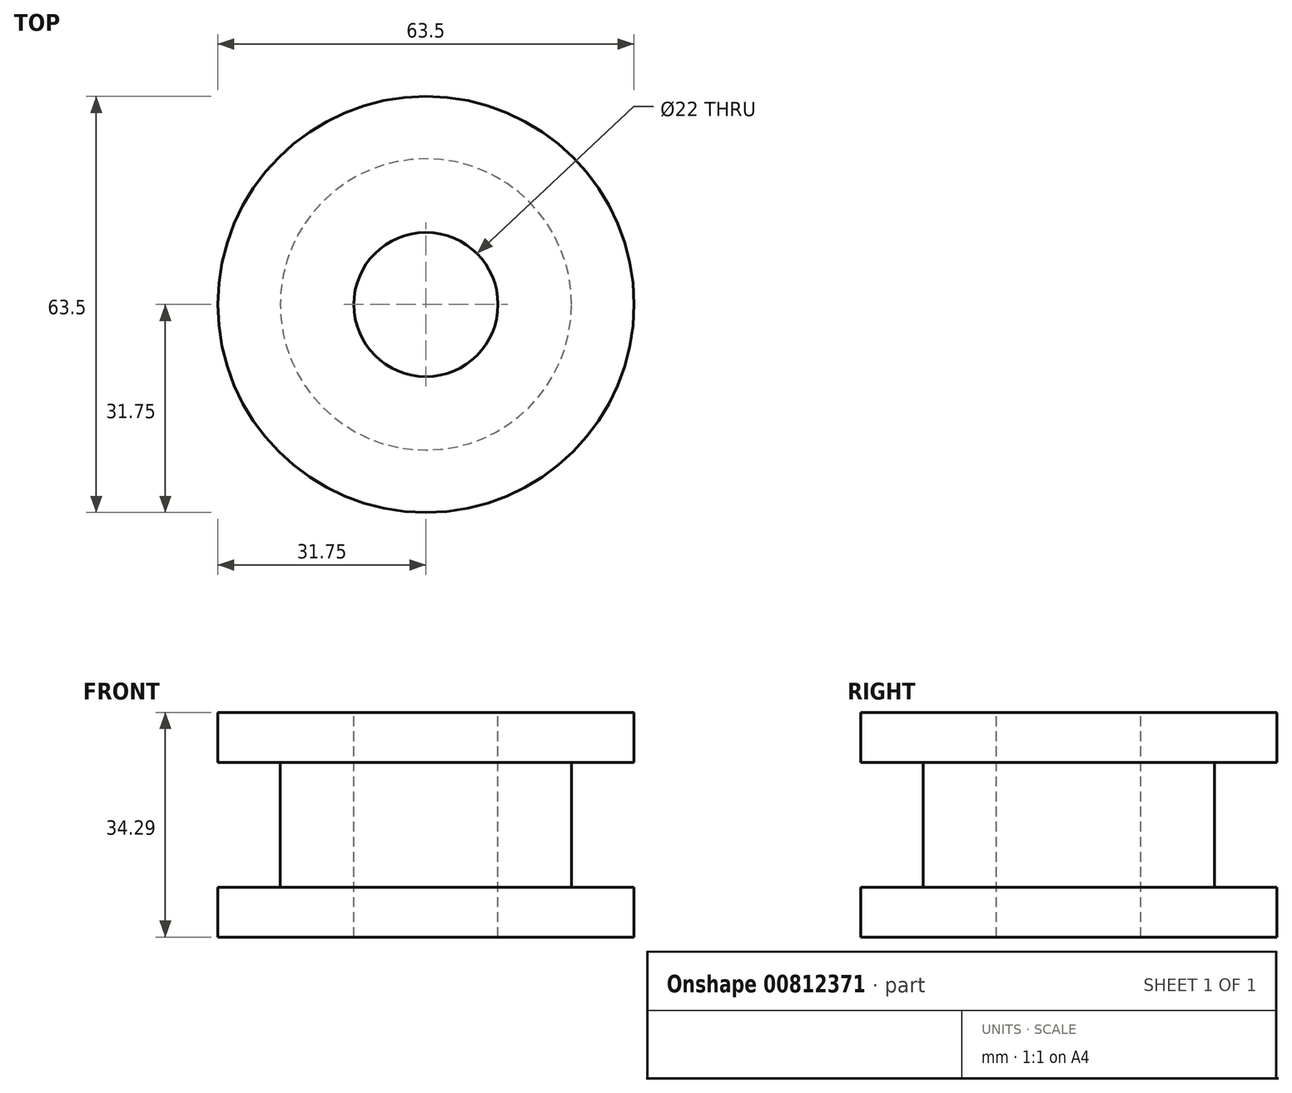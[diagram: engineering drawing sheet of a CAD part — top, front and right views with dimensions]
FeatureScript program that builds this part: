
annotation { "Feature Type Name" : "Feature", "Feature Type Description" : "" }
export const myFeature = defineFeature(function(context is Context, id is Id, definition is map)
    precondition{}
    {
        {
            var Q0;
            Q0=qCreatedBy(makeId("Top.planeOp"),FACE);
            var sketch = newSketch(context, id + "F0", { "sketchPlane" : qUnion([Q0])});
            skCircle(sketch, "E0", {"center": v(0, 0) * mm, "radius": 31.75 * mm});
            skSolve(sketch);
        }
        {
            var Q0;
            Q0=makeQuery(id+"F0.imprint","IMPRINT",FACE,{"disambiguationData":[TD([[makeQuery(id+"F0.imprint","IMPRINT",EDGE,{"derivedFrom":sQuery(id+"F0.wireOp",EDGE,"E0")}),1.0]])]});
            extrude(context, id + "F1", {"entities" : qUnion([Q0]), "depth" : 7.62 * mm, "offsetDistance" : 25.4 * mm});
        }
        {
            var Q0;
            Q0=makeQuery(id+"F1.opExtrude","CAP_FACE",FACE,{"disambiguationData":[OSD([sQuery(id+"F0.wireOp",EDGE,"E0")])],"isStart":false});
            var sketch = newSketch(context, id + "F2", { "sketchPlane" : qUnion([Q0])});
            skCircle(sketch, "E1", {"center": v(0, 0) * mm, "radius": 22.23 * mm});
            skSolve(sketch);
        }
        {
            var Q0;
            Q0=makeQuery(id+"F2.imprint","IMPRINT",FACE,{"disambiguationData":[TD([[makeQuery(id+"F2.imprint","IMPRINT",EDGE,{"derivedFrom":sQuery(id+"F2.wireOp",EDGE,"E1")}),1.0]])]});
            extrude(context, id + "F3", {"entities" : qUnion([Q0]), "operationType" : NewBodyOperationType.ADD, "depth" : 19.05 * mm, "offsetDistance" : 25.4 * mm});
        }
        {
            var Q0;
            Q0=makeQuery(id+"F3.opExtrude","CAP_FACE",FACE,{"disambiguationData":[OSD([sQuery(id+"F2.wireOp",EDGE,"E1")])],"isStart":false});
            var sketch = newSketch(context, id + "F4", { "sketchPlane" : qUnion([Q0])});
            skCircle(sketch, "E2", {"center": v(0, 0) * mm, "radius": 31.75 * mm});
            skSolve(sketch);
        }
        {
            var Q0;
            Q0 = qSketchRegion(id + "F4", true);
            extrude(context, id + "F5", {"entities" : qUnion([Q0]), "operationType" : NewBodyOperationType.ADD, "depth" : 7.62 * mm, "offsetDistance" : 25.4 * mm});
        }
        {
            var Q0;
            Q0=makeQuery(id+"F5.opExtrude","CAP_FACE",FACE,{"disambiguationData":[OSD([sQuery(id+"F4.wireOp",EDGE,"E2")])],"isStart":false});
            var sketch = newSketch(context, id + "F6", { "sketchPlane" : qUnion([Q0])});
            skCircle(sketch, "E3", {"center": v(0, 0) * mm, "radius": 11 * mm});
            skSolve(sketch);
        }
        {
            var Q0;
            Q0 = qSketchRegion(id + "F6", true);
            extrude(context, id + "F7", {"entities" : qUnion([Q0]), "operationType" : NewBodyOperationType.REMOVE, "oppositeDirection" : true, "depth" : 56.13 * mm, "offsetDistance" : 25.4 * mm});
        }
    });
